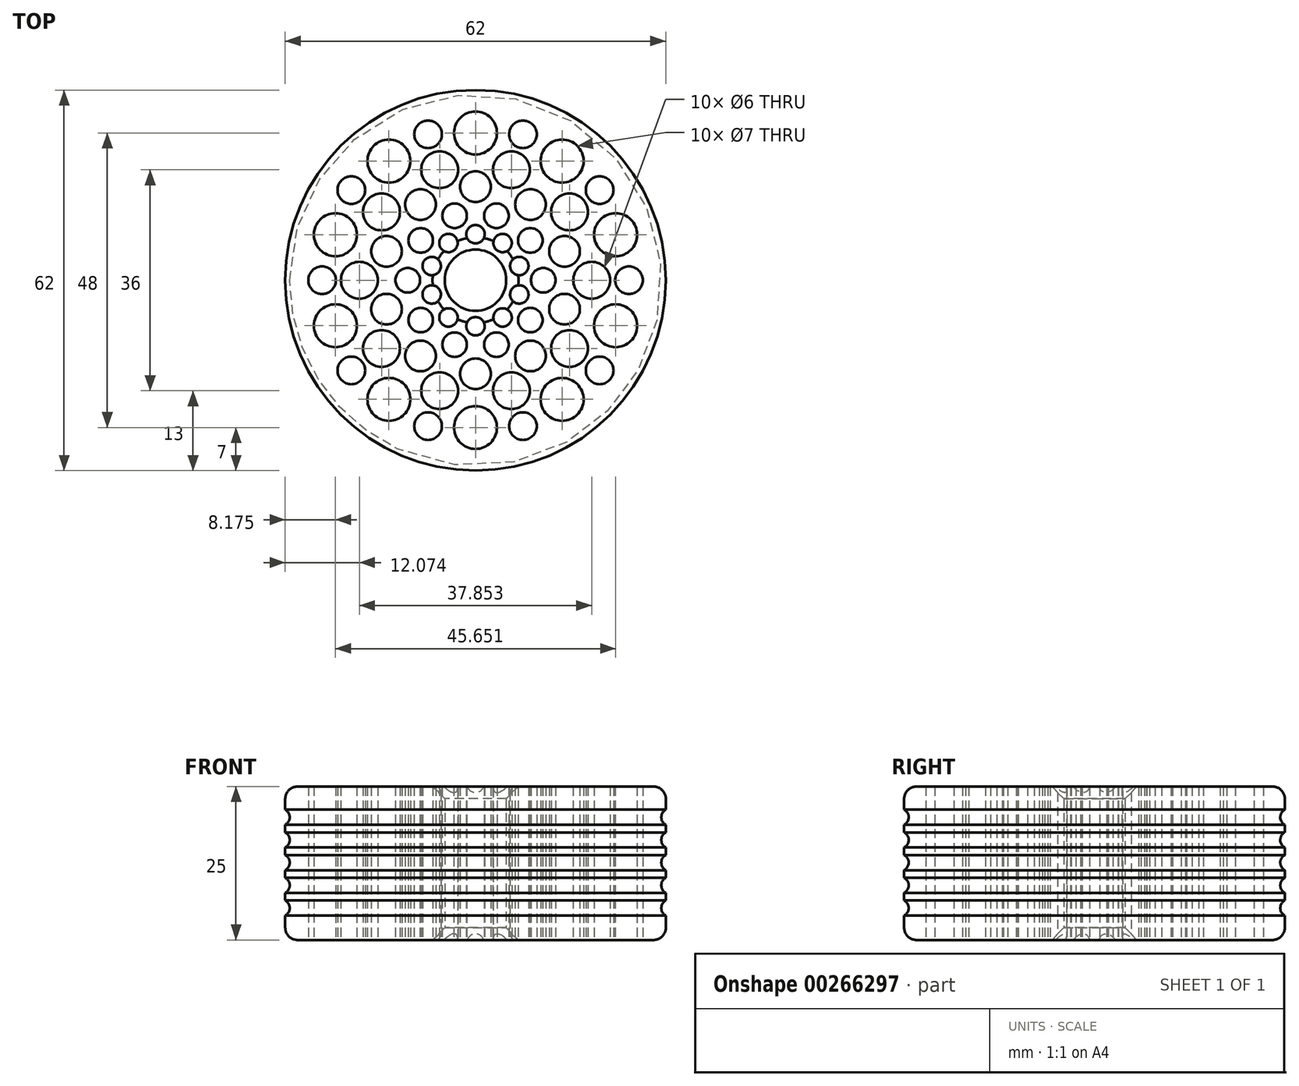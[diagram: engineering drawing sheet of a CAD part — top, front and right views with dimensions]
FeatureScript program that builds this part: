
annotation { "Feature Type Name" : "Feature", "Feature Type Description" : "" }
export const myFeature = defineFeature(function(context is Context, id is Id, definition is map)
    precondition{}
    {
        {
            var Q0;
            Q0=qCreatedBy(makeId("Top.planeOp"),FACE);
            var sketch = newSketch(context, id + "F0", { "sketchPlane" : qUnion([Q0])});
            skCircle(sketch, "E0", {"center": v(0, 0) * mm, "radius": 31 * mm});
            skCircle(sketch, "E1", {"center": v(0, 0) * mm, "radius": 5 * mm});
            skLineSegment(sketch, "E2", {"start": v(0, 27.98) * mm, "end": v(0, -28.24) * mm, "construction": true});
            skLineSegment(sketch, "E3", {"start": v(-27.85, 0) * mm, "end": v(29.26, 0) * mm, "construction": true});
            skCircle(sketch, "E4", {"center": v(0, 7.5) * mm, "radius": 1.5 * mm});
            skCircle(sketch, "E5.1.0", {"center": v(4.4, 6.07) * mm, "radius": 1.5 * mm});
            skCircle(sketch, "E5.2.0", {"center": v(7.13, 2.32) * mm, "radius": 1.5 * mm});
            skCircle(sketch, "E5.3.0", {"center": v(7.13, -2.32) * mm, "radius": 1.5 * mm});
            skCircle(sketch, "E5.4.0", {"center": v(4.4, -6.07) * mm, "radius": 1.5 * mm});
            skCircle(sketch, "E5.5.0", {"center": v(0, -7.5) * mm, "radius": 1.5 * mm});
            skCircle(sketch, "E5.6.0", {"center": v(-4.4, -6.07) * mm, "radius": 1.5 * mm});
            skCircle(sketch, "E5.7.0", {"center": v(-7.13, -2.32) * mm, "radius": 1.5 * mm});
            skCircle(sketch, "E5.8.0", {"center": v(-7.13, 2.32) * mm, "radius": 1.5 * mm});
            skLineSegment(sketch, "E5.anchor1", {"start": v(0, 0) * mm, "end": v(0, 7.5) * mm, "construction": true});
            skLineSegment(sketch, "E5.anchor2", {"start": v(0, 0) * mm, "end": v(-4.4, 6.07) * mm, "construction": true});
            skLineSegment(sketch, "E6", {"start": v(0, 0) * mm, "end": v(-9.58, 29.48) * mm, "construction": true});
            skCircle(sketch, "E7", {"center": v(-3.41, 10.5) * mm, "radius": 2 * mm});
            skCircle(sketch, "E8.1.0", {"center": v(3.41, 10.5) * mm, "radius": 2 * mm});
            skCircle(sketch, "E8.2.0", {"center": v(8.93, 6.49) * mm, "radius": 2 * mm});
            skCircle(sketch, "E8.3.0", {"center": v(11.04, 0) * mm, "radius": 2 * mm});
            skCircle(sketch, "E8.4.0", {"center": v(8.93, -6.49) * mm, "radius": 2 * mm});
            skCircle(sketch, "E8.5.0", {"center": v(3.41, -10.5) * mm, "radius": 2 * mm});
            skCircle(sketch, "E8.6.0", {"center": v(-3.41, -10.5) * mm, "radius": 2 * mm});
            skCircle(sketch, "E8.7.0", {"center": v(-8.93, -6.49) * mm, "radius": 2 * mm});
            skCircle(sketch, "E8.8.0", {"center": v(-11.04, 0) * mm, "radius": 2 * mm});
            skCircle(sketch, "E8.9.0", {"center": v(-8.93, 6.49) * mm, "radius": 2 * mm});
            skLineSegment(sketch, "E8.anchor1", {"start": v(0, 0) * mm, "end": v(-3.41, 10.5) * mm, "construction": true});
            skLineSegment(sketch, "E8.anchor2", {"start": v(0, 0) * mm, "end": v(-8.93, 6.49) * mm, "construction": true});
            skCircle(sketch, "E9", {"center": v(0, 15.25) * mm, "radius": 2.5 * mm});
            skCircle(sketch, "E10.1.9.0", {"center": v(-4.4, 6.07) * mm, "radius": 1.5 * mm});
            skCircle(sketch, "E11.1.0", {"center": v(-8.96, 12.34) * mm, "radius": 2.5 * mm});
            skCircle(sketch, "E11.2.0", {"center": v(-14.5, 4.71) * mm, "radius": 2.5 * mm});
            skCircle(sketch, "E11.3.0", {"center": v(-14.5, -4.71) * mm, "radius": 2.5 * mm});
            skCircle(sketch, "E11.4.0", {"center": v(-8.96, -12.34) * mm, "radius": 2.5 * mm});
            skCircle(sketch, "E11.5.0", {"center": v(0, -15.25) * mm, "radius": 2.5 * mm});
            skCircle(sketch, "E11.6.0", {"center": v(8.96, -12.34) * mm, "radius": 2.5 * mm});
            skCircle(sketch, "E11.7.0", {"center": v(14.5, -4.71) * mm, "radius": 2.5 * mm});
            skCircle(sketch, "E11.8.0", {"center": v(14.5, 4.71) * mm, "radius": 2.5 * mm});
            skCircle(sketch, "E11.9.0", {"center": v(8.96, 12.34) * mm, "radius": 2.5 * mm});
            skCircle(sketch, "E12", {"center": v(-5.85, 18) * mm, "radius": 3 * mm});
            skCircle(sketch, "E13.1.0", {"center": v(-15.31, 11.12) * mm, "radius": 3 * mm});
            skCircle(sketch, "E13.2.0", {"center": v(-18.93, 0) * mm, "radius": 3 * mm});
            skCircle(sketch, "E13.3.0", {"center": v(-15.31, -11.12) * mm, "radius": 3 * mm});
            skCircle(sketch, "E13.4.0", {"center": v(-5.85, -18) * mm, "radius": 3 * mm});
            skCircle(sketch, "E13.5.0", {"center": v(5.85, -18) * mm, "radius": 3 * mm});
            skCircle(sketch, "E13.6.0", {"center": v(15.31, -11.12) * mm, "radius": 3 * mm});
            skCircle(sketch, "E13.7.0", {"center": v(18.93, 0) * mm, "radius": 3 * mm});
            skCircle(sketch, "E13.8.0", {"center": v(15.31, 11.12) * mm, "radius": 3 * mm});
            skCircle(sketch, "E13.9.0", {"center": v(5.85, 18) * mm, "radius": 3 * mm});
            skCircle(sketch, "E14", {"center": v(0, 24) * mm, "radius": 3.5 * mm});
            skCircle(sketch, "E15.1.0", {"center": v(-14.1, 19.42) * mm, "radius": 3.5 * mm});
            skCircle(sketch, "E15.2.0", {"center": v(-22.83, 7.42) * mm, "radius": 3.5 * mm});
            skCircle(sketch, "E15.3.0", {"center": v(-22.83, -7.42) * mm, "radius": 3.5 * mm});
            skCircle(sketch, "E15.4.0", {"center": v(-14.1, -19.42) * mm, "radius": 3.5 * mm});
            skCircle(sketch, "E15.5.0", {"center": v(0, -24) * mm, "radius": 3.5 * mm});
            skCircle(sketch, "E15.6.0", {"center": v(14.1, -19.42) * mm, "radius": 3.5 * mm});
            skCircle(sketch, "E15.7.0", {"center": v(22.83, -7.42) * mm, "radius": 3.5 * mm});
            skCircle(sketch, "E15.8.0", {"center": v(22.83, 7.42) * mm, "radius": 3.5 * mm});
            skCircle(sketch, "E15.9.0", {"center": v(14.1, 19.42) * mm, "radius": 3.5 * mm});
            skCircle(sketch, "E16", {"center": v(-7.73, 23.78) * mm, "radius": 2.25 * mm});
            skCircle(sketch, "E17.1.0", {"center": v(-20.23, 14.7) * mm, "radius": 2.25 * mm});
            skCircle(sketch, "E17.2.0", {"center": v(-25, 0) * mm, "radius": 2.25 * mm});
            skCircle(sketch, "E17.3.0", {"center": v(-20.23, -14.7) * mm, "radius": 2.25 * mm});
            skCircle(sketch, "E17.4.0", {"center": v(-7.73, -23.78) * mm, "radius": 2.25 * mm});
            skCircle(sketch, "E17.5.0", {"center": v(7.73, -23.78) * mm, "radius": 2.25 * mm});
            skCircle(sketch, "E17.6.0", {"center": v(20.23, -14.7) * mm, "radius": 2.25 * mm});
            skCircle(sketch, "E17.7.0", {"center": v(25, 0) * mm, "radius": 2.25 * mm});
            skCircle(sketch, "E17.8.0", {"center": v(20.23, 14.7) * mm, "radius": 2.25 * mm});
            skCircle(sketch, "E17.9.0", {"center": v(7.73, 23.78) * mm, "radius": 2.25 * mm});
            skSolve(sketch);
        }
        {
            var Q0;
            Q0 = qSketchRegion(id + "F0", true);
            extrude(context, id + "F1", {"entities" : qUnion([Q0]), "endBound" : BoundingType.SYMMETRIC, "depth" : 25 * mm});
        }
        {
            var Q0;
            Q0=makeQuery(id+"F1.opExtrude","CAP_EDGE",EDGE,{"disambiguationData":[OSD([sQuery(id+"F0.wireOp",EDGE,"E0")])],"isStart":false});
            var Q1;
            Q1=makeQuery(id+"F1.opExtrude","CAP_EDGE",EDGE,{"disambiguationData":[OSD([sQuery(id+"F0.wireOp",EDGE,"E0")])],"isStart":true});
            fillet(context, id + "F2", {"entities" : qUnion([Q0, Q1]), "radius" : 2 * mm, "tangentPropagation" : true, "allowEdgeOverflow" : false});
        }
        {
            var Q0;
            Q0=qCreatedBy(makeId("Right.planeOp"),FACE);
            var sketch = newSketch(context, id + "F3", { "sketchPlane" : qUnion([Q0])});
            skLineSegment(sketch, "E18", {"start": v(0, 25.5) * mm, "end": v(0, -32.54) * mm, "construction": true});
            skCircle(sketch, "E19", {"center": v(31.67, 7.5) * mm, "radius": 1.4 * mm});
            skCircle(sketch, "E20.0.1.0", {"center": v(31.67, 3.8) * mm, "radius": 1.4 * mm});
            skCircle(sketch, "E20.0.2.0", {"center": v(31.67, 0.1) * mm, "radius": 1.4 * mm});
            skCircle(sketch, "E20.0.3.0", {"center": v(31.67, -3.6) * mm, "radius": 1.4 * mm});
            skCircle(sketch, "E20.0.4.0", {"center": v(31.67, -7.3) * mm, "radius": 1.4 * mm});
            skLineSegment(sketch, "E20.direction1", {"start": v(31.67, 7.5) * mm, "end": v(56.67, 7.5) * mm, "construction": true});
            skLineSegment(sketch, "E20.direction2", {"start": v(31.67, 7.5) * mm, "end": v(31.67, 3.8) * mm, "construction": true});
            skSolve(sketch);
        }
        {
            var Q0;
            Q0=makeQuery(id+"F3.imprint","IMPRINT",FACE,{"disambiguationData":[TD([[makeQuery(id+"F3.imprint","IMPRINT",EDGE,{"derivedFrom":sQuery(id+"F3.wireOp",EDGE,"E20.0.1.0")}),1.0]])]});
            var Q1;
            Q1=makeQuery(id+"F3.imprint","IMPRINT",FACE,{"disambiguationData":[TD([[makeQuery(id+"F3.imprint","IMPRINT",EDGE,{"derivedFrom":sQuery(id+"F3.wireOp",EDGE,"E19")}),1.0]])]});
            var Q2;
            Q2=makeQuery(id+"F3.imprint","IMPRINT",FACE,{"disambiguationData":[TD([[makeQuery(id+"F3.imprint","IMPRINT",EDGE,{"derivedFrom":sQuery(id+"F3.wireOp",EDGE,"E20.0.4.0")}),1.0]])]});
            var Q3;
            Q3=makeQuery(id+"F3.imprint","IMPRINT",FACE,{"disambiguationData":[TD([[makeQuery(id+"F3.imprint","IMPRINT",EDGE,{"derivedFrom":sQuery(id+"F3.wireOp",EDGE,"E20.0.3.0")}),1.0]])]});
            var Q4;
            Q4=makeQuery(id+"F3.imprint","IMPRINT",FACE,{"disambiguationData":[TD([[makeQuery(id+"F3.imprint","IMPRINT",EDGE,{"derivedFrom":sQuery(id+"F3.wireOp",EDGE,"E20.0.2.0")}),1.0]])]});
            var Q5;
            Q5=sQuery(id+"F3.wireOp",EDGE,"E18");
            revolve(context, id + "F4", {"operationType" : NewBodyOperationType.REMOVE, "entities" : qUnion([Q0, Q1, Q2, Q3, Q4]), "axis" : qUnion([Q5]), "revolveType" : RevolveType.FULL, "oppositeDirection" : true});
        }
        {
            var Q0;
            Q0=makeQuery(id+"F1.opExtrude","CAP_EDGE",EDGE,{"disambiguationData":[OSD([sQuery(id+"F0.wireOp",EDGE,"E1")])],"isStart":false});
            var Q1;
            Q1=makeQuery(id+"F1.opExtrude","CAP_EDGE",EDGE,{"disambiguationData":[OSD([sQuery(id+"F0.wireOp",EDGE,"E1")])],"isStart":true});
            chamfer(context, id + "F5", {"entities" : qUnion([Q0, Q1]), "width" : 2 * mm, "tangentPropagation" : true});
        }
    });
